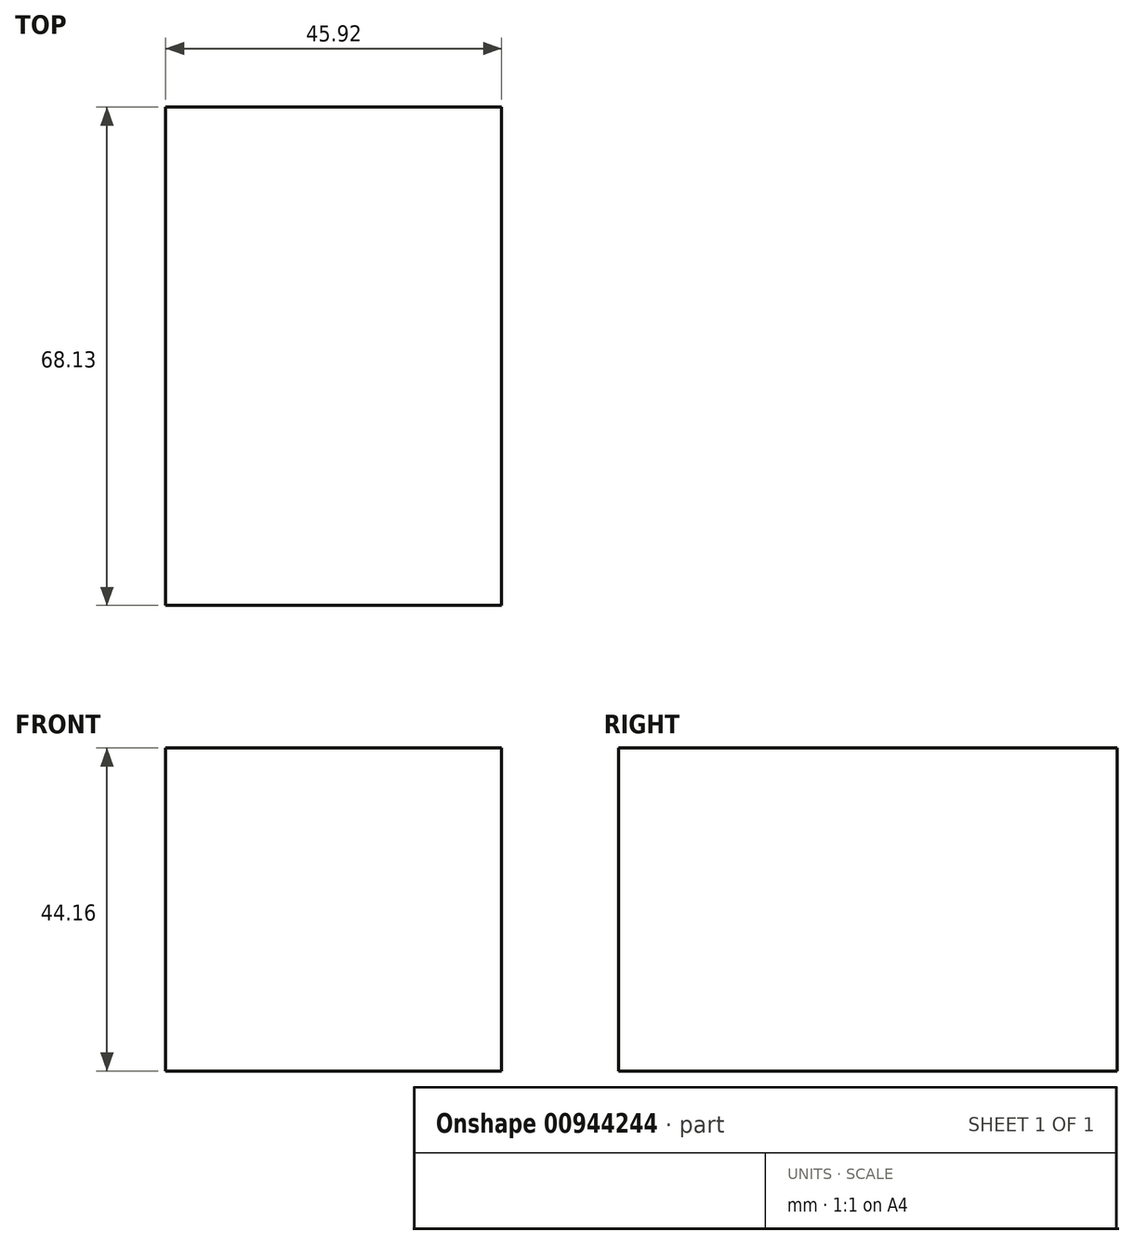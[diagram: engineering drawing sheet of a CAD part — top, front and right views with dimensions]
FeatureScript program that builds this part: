
annotation { "Feature Type Name" : "Feature", "Feature Type Description" : "" }
export const myFeature = defineFeature(function(context is Context, id is Id, definition is map)
    precondition{}
    {
        {
            var Q0;
            Q0=qCreatedBy(makeId("Front.planeOp"),FACE);
            var sketch = newSketch(context, id + "F0", { "sketchPlane" : qUnion([Q0])});
            skLineSegment(sketch, "E0.bottom", {"start": v(45.92, 7.9) * mm, "end": v(0, 7.9) * mm});
            skLineSegment(sketch, "E0.top", {"start": v(45.92, 52.05) * mm, "end": v(0, 52.05) * mm});
            skLineSegment(sketch, "E0.left", {"start": v(45.92, 7.9) * mm, "end": v(45.92, 52.05) * mm});
            skLineSegment(sketch, "E0.right", {"start": v(0, 7.9) * mm, "end": v(0, 52.05) * mm});
            skSolve(sketch);
        }
        {
            var Q0;
            Q0=sQuery(id+"F0.wireOp",EDGE,"E0.left");
            var Q1;
            Q1=sQuery(id+"F0.wireOp",EDGE,"E0.top");
            var Q2;
            Q2=sQuery(id+"F0.wireOp",EDGE,"E0.right");
            var Q3;
            Q3=sQuery(id+"F0.wireOp",EDGE,"E0.bottom");
            extrude(context, id + "F1", {"bodyType" : ToolBodyType.SURFACE, "surfaceEntities" : qUnion([Q0, Q1, Q2, Q3]), "depth" : 68.13 * mm, "offsetDistance" : 25 * mm});
        }
    });
